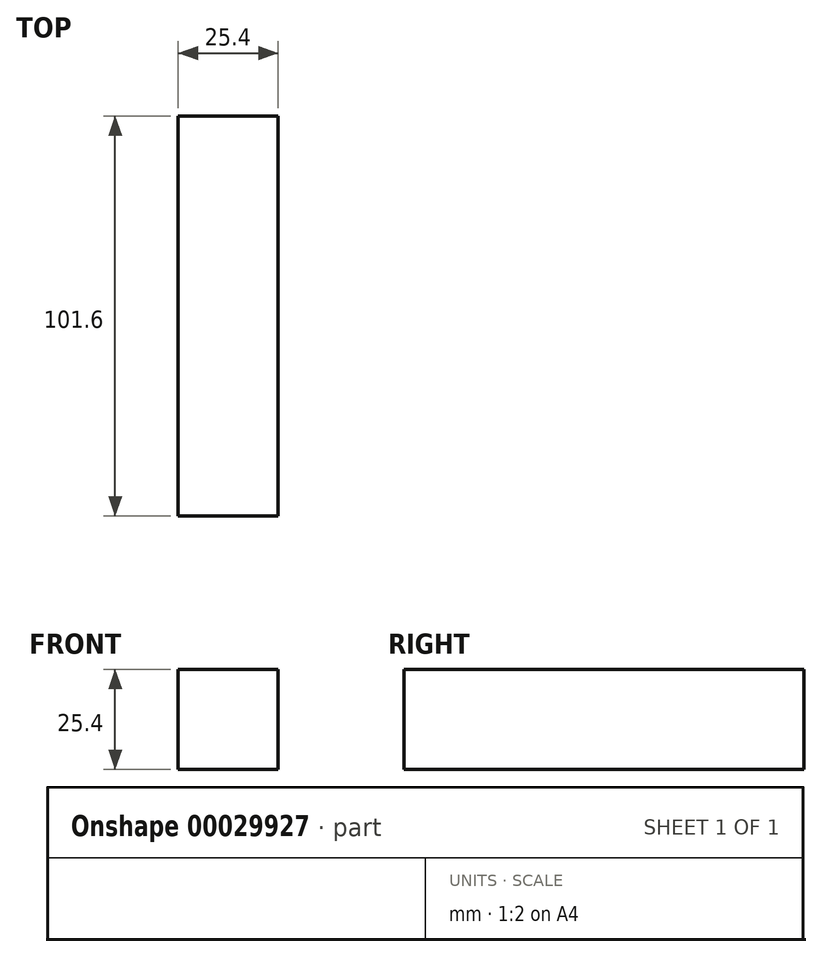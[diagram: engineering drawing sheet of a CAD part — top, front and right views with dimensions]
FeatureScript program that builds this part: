
annotation { "Feature Type Name" : "Feature", "Feature Type Description" : "" }
export const myFeature = defineFeature(function(context is Context, id is Id, definition is map)
    precondition{}
    {
        {
            var Q0;
            Q0=qCreatedBy(makeId("Front.planeOp"),FACE);
            var sketch = newSketch(context, id + "F0", { "sketchPlane" : qUnion([Q0])});
            skLineSegment(sketch, "E0.bottom", {"start": v(-17.82, 24.94) * mm, "end": v(7.58, 24.94) * mm});
            skLineSegment(sketch, "E0.top", {"start": v(-17.82, -0.46) * mm, "end": v(7.58, -0.46) * mm});
            skLineSegment(sketch, "E0.left", {"start": v(-17.82, 24.94) * mm, "end": v(-17.82, -0.46) * mm});
            skLineSegment(sketch, "E0.right", {"start": v(7.58, 24.94) * mm, "end": v(7.58, -0.46) * mm});
            skSolve(sketch);
        }
        {
            var Q0;
            Q0=makeQuery(id+"F0.imprint","IMPRINT",FACE,{"disambiguationData":[TD([[makeQuery(id+"F0.imprint","IMPRINT",EDGE,{"derivedFrom":sQuery(id+"F0.wireOp",EDGE,"E0.bottom")}),-1.0]])]});
            extrude(context, id + "F1", {"entities" : qUnion([Q0]), "depth" : 101.6 * mm});
        }
    });
